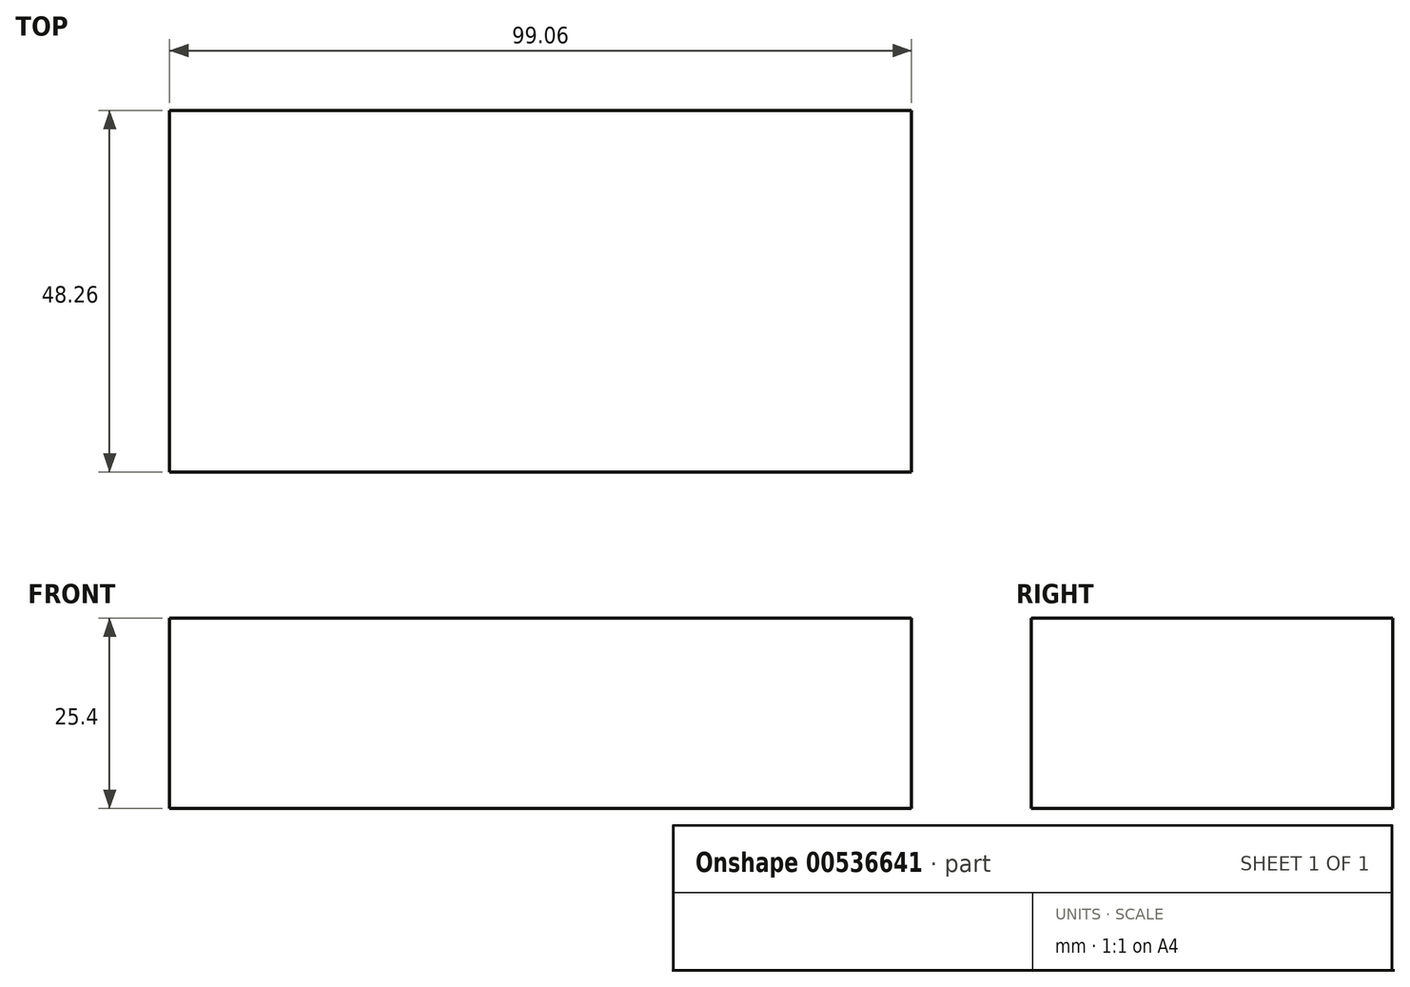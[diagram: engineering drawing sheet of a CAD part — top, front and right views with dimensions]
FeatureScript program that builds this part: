
annotation { "Feature Type Name" : "Feature", "Feature Type Description" : "" }
export const myFeature = defineFeature(function(context is Context, id is Id, definition is map)
    precondition{}
    {
        {
            var Q0;
            Q0=qCreatedBy(makeId("Top.planeOp"),FACE);
            var sketch = newSketch(context, id + "F0", { "sketchPlane" : qUnion([Q0])});
            skLineSegment(sketch, "E0.bottom", {"start": v(-50.8, 25.4) * mm, "end": v(50.8, 25.4) * mm});
            skLineSegment(sketch, "E0.top", {"start": v(-50.8, -25.4) * mm, "end": v(50.8, -25.4) * mm});
            skLineSegment(sketch, "E0.left", {"start": v(-50.8, 25.4) * mm, "end": v(-50.8, -25.4) * mm});
            skLineSegment(sketch, "E0.right", {"start": v(50.8, 25.4) * mm, "end": v(50.8, -25.4) * mm});
            skPoint(sketch, "E0.middle", {"position": v(0, 0) * mm});
            skLineSegment(sketch, "E1", {"start": v(-49.3, -25.4) * mm, "end": v(-49.3, 22.86) * mm});
            skLineSegment(sketch, "E2", {"start": v(-49.3, 22.86) * mm, "end": v(49.76, 22.86) * mm});
            skLineSegment(sketch, "E3", {"start": v(49.76, 22.86) * mm, "end": v(49.76, -25.4) * mm});
            skSolve(sketch);
        }
        {
            var Q0;
            {var subQ0=sQuery(id+"F0.wireOp",EDGE,"E1");Q0=makeQuery(id+"F0.imprint","IMPRINT",FACE,{"disambiguationData":[TD([[makeQuery(id+"F0.imprint","IMPRINT",EDGE,{"derivedFrom":subQ0}),-1.0]])]});}
            extrude(context, id + "F1", {"entities" : qUnion([Q0]), "depth" : 25.4 * mm, "offsetDistance" : 25.4 * mm});
        }
    });
